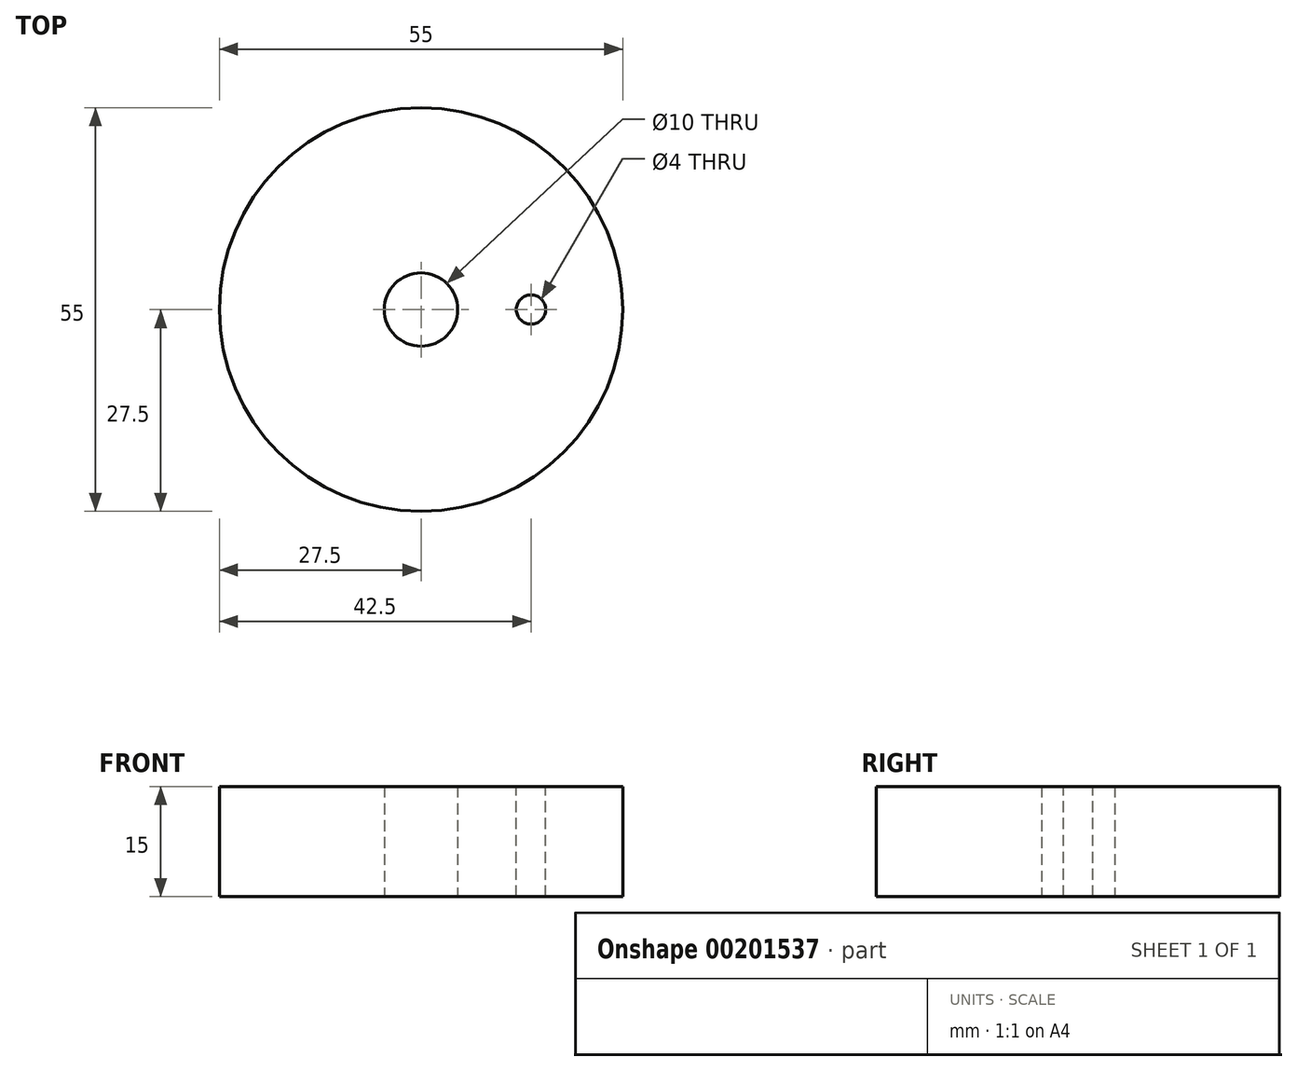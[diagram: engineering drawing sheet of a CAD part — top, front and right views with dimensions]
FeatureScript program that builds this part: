
annotation { "Feature Type Name" : "Feature", "Feature Type Description" : "" }
export const myFeature = defineFeature(function(context is Context, id is Id, definition is map)
    precondition{}
    {
        {
            var Q0;
            Q0=qCreatedBy(makeId("Top.planeOp"),FACE);
            var sketch = newSketch(context, id + "F0", { "sketchPlane" : qUnion([Q0])});
            skCircle(sketch, "E0", {"center": v(0, 0) * mm, "radius": 5 * mm});
            skCircle(sketch, "E1", {"center": v(0, 0) * mm, "radius": 27.5 * mm});
            skSolve(sketch);
        }
        {
            var Q0;
            Q0=makeQuery(id+"F0.imprint","IMPRINT",FACE,{"disambiguationData":[TD([[makeQuery(id+"F0.imprint","IMPRINT",EDGE,{"derivedFrom":sQuery(id+"F0.wireOp",EDGE,"E0")}),-1.0]])]});
            extrude(context, id + "F1", {"entities" : qUnion([Q0]), "depth" : 15 * mm});
        }
        {
            var Q0;
            Q0=makeQuery(id+"F1.opExtrude","CAP_FACE",FACE,{"disambiguationData":[OSD([sQuery(id+"F0.wireOp",EDGE,"E0"),sQuery(id+"F0.wireOp",EDGE,"E1")])],"isStart":false});
            var sketch = newSketch(context, id + "F2", { "sketchPlane" : qUnion([Q0])});
            skCircle(sketch, "E2", {"center": v(15, 0) * mm, "radius": 2 * mm});
            skSolve(sketch);
        }
        {
            var Q0;
            Q0 = qSketchRegion(id + "F2", true);
            extrude(context, id + "F3", {"entities" : qUnion([Q0]), "operationType" : NewBodyOperationType.REMOVE, "endBound" : BoundingType.THROUGH_ALL, "oppositeDirection" : true, "depth" : 25 * mm});
        }
    });
